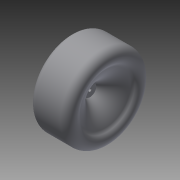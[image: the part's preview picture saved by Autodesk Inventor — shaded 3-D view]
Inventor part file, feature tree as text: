
AUTODESK INVENTOR PART (.ipt)
format: ipt  version: 2015 (Build 190159000, 159)  size: 201,728 bytes
history: native  units: mm
features: fillet x4, sketch x2, revolve x1, extrude x1
ambient origin geometry x8: Origin, YZ Plane, XZ Plane, XY Plane, X Axis, Y Axis, Z Axis, Center Point
bodies: Solid1 (feature_tree)
feature tree (8):
  revolve  "Revolution1"  [1 undecoded]
  extrude  "Extrusion1"  Depth=10.25mm
  fillet  "Fillet1"  Radius=10.0mm
  fillet  "Fillet2"  Radius=10.0mm
  fillet  "Fillet3"  Radius=9.25mm
  fillet  "Fillet4"  Radius=11.25mm
  sketch  "Sketch1"  dims[d9=4.0mm d12=5.0mm]
  sketch  "Sketch2"  dims[d15=90.0deg d16=4.2mm d17=10.0mm d18=0.0mm d19=10.0mm d20=9.25mm d21=11.25mm d22=10.25mm]
note: 1 required parameter value undecoded (feature->parameter linkage not recoverable at this tier; creation-order binding heuristic only, values carry confidence <= 0.55)
